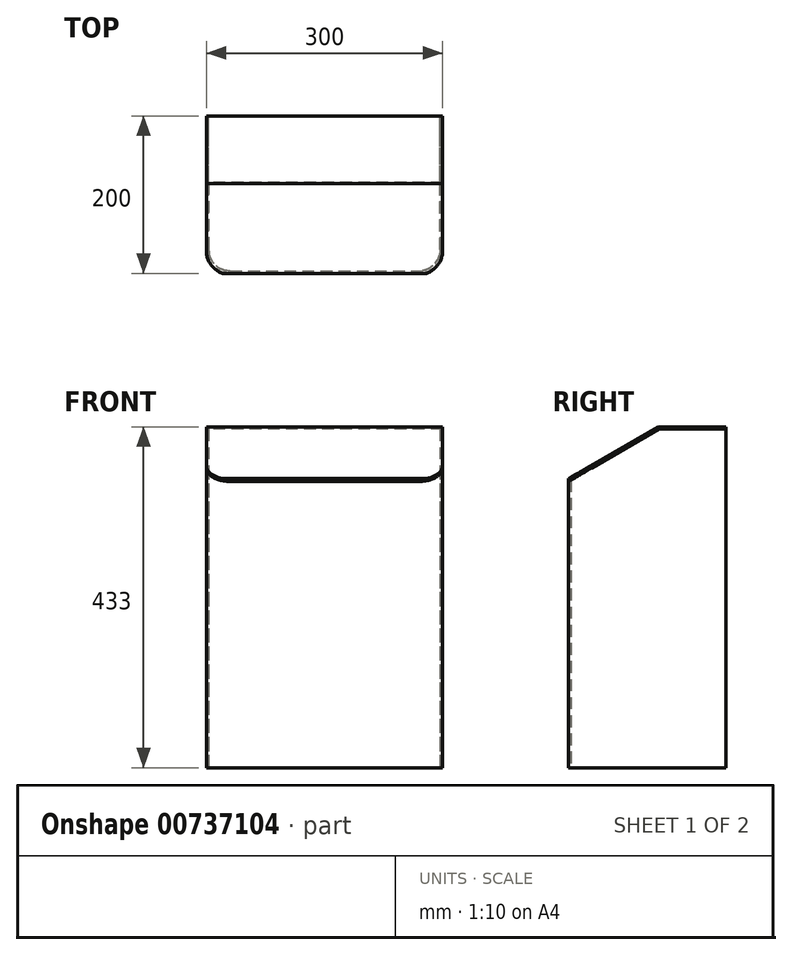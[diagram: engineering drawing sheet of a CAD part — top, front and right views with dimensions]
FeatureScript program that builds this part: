
annotation { "Feature Type Name" : "Feature", "Feature Type Description" : "" }
export const myFeature = defineFeature(function(context is Context, id is Id, definition is map)
    precondition{}
    {
        {
            var Q0;
            Q0=qCreatedBy(makeId("Top.planeOp"),FACE);
            var sketch = newSketch(context, id + "F0", { "sketchPlane" : qUnion([Q0])});
            skLineSegment(sketch, "E0", {"start": v(-30, 0) * mm, "end": v(-270, 0) * mm});
            skLineSegment(sketch, "E1", {"start": v(-300, 30) * mm, "end": v(-300, 200) * mm});
            skLineSegment(sketch, "E2", {"start": v(0, 30) * mm, "end": v(0, 200) * mm});
            skPoint(sketch, "E3.visualSharp", {"position": v(-300, 0) * mm});
            skArc(sketch, "E3.filletArc", {"start": v(-300, 30) * mm, "mid": v(-291.21, 8.79) * mm, "end": v(-270, 0) * mm});
            skPoint(sketch, "E4.visualSharp", {"position": v(0, 0) * mm});
            skArc(sketch, "E4.filletArc", {"start": v(-30, 0) * mm, "mid": v(-8.79, 8.79) * mm, "end": v(0, 30) * mm});
            skLineSegment(sketch, "E5.0", {"start": v(-297, 30) * mm, "end": v(-297, 200) * mm});
            skLineSegment(sketch, "E5.1", {"start": v(-3, 30) * mm, "end": v(-3, 200) * mm});
            skArc(sketch, "E5.2", {"start": v(-30, 3) * mm, "mid": v(-10.9, 10.9) * mm, "end": v(-3, 30) * mm});
            skLineSegment(sketch, "E5.3", {"start": v(-30, 3) * mm, "end": v(-270, 3) * mm});
            skArc(sketch, "E5.4", {"start": v(-297, 30) * mm, "mid": v(-289.1, 10.9) * mm, "end": v(-270, 3) * mm});
            skLineSegment(sketch, "E6", {"start": v(-300, 200) * mm, "end": v(-297, 200) * mm});
            skLineSegment(sketch, "E7", {"start": v(0, 200) * mm, "end": v(-3, 200) * mm});
            skSolve(sketch);
        }
        {
            var Q0;
            Q0=makeQuery(id+"F0.imprint","IMPRINT",FACE,{"disambiguationData":[TD([[makeQuery(id+"F0.imprint","IMPRINT",EDGE,{"derivedFrom":sQuery(id+"F0.wireOp",EDGE,"E0")}),-1.0]])]});
            extrude(context, id + "F1", {"entities" : qUnion([Q0]), "depth" : 430 * mm, "offsetDistance" : 25 * mm});
        }
        {
            var Q0;
            Q0=makeQuery(id+"F1.opExtrude","SWEPT_FACE",FACE,{"disambiguationData":[OSD([sQuery(id+"F0.wireOp",EDGE,"E1")])]});
            var sketch = newSketch(context, id + "F2", { "sketchPlane" : qUnion([Q0])});
            skLineSegment(sketch, "E8", {"start": v(-115, 430) * mm, "end": v(118.7, 430) * mm});
            skLineSegment(sketch, "E9", {"start": v(-115, 430) * mm, "end": v(118.7, 295.08) * mm});
            skLineSegment(sketch, "E10", {"start": v(118.7, 295.08) * mm, "end": v(118.7, 430) * mm});
            skSolve(sketch);
        }
        {
            var Q0;
            {var subQ3=sQuery(id+"F2.wireOp",EDGE,"E10");Q0=makeQuery(id+"F2.imprint","IMPRINT",FACE,{"disambiguationData":[TD([[makeQuery(id+"F2.imprint","IMPRINT",EDGE,{"derivedFrom":subQ3}),1.0]])]});}
            var Q1;
            {var subQ0=sQuery(id+"F2.wireOp",EDGE,"E8");var subQ1=sQuery(id+"F0.wireOp",EDGE,"E1");var subQ4=sQuery(id+"F2.wireOp",EDGE,"E9");var subQ5=makeQuery(id+"F2.imprint","INTERSECT",VERTEX,{"derivedFrom":[makeQuery(id+"F1.opExtrude","CAP_EDGE",EDGE,{"disambiguationData":[OSD([subQ1])],"isStart":false}),subQ0,subQ4]});Q1=makeQuery(id+"F2.imprint","IMPRINT",FACE,{"disambiguationData":[TD([[makeQuery(id+"F2.imprint","IMPRINT",EDGE,{"disambiguationData":[TD([[subQ5,1.0]])],"derivedFrom":subQ0}),1.0]])]});}
            extrude(context, id + "F3", {"entities" : qUnion([Q0, Q1]), "operationType" : NewBodyOperationType.REMOVE, "oppositeDirection" : true, "depth" : 455 * mm, "offsetDistance" : 25 * mm});
        }
        {
            var Q0;
            Q0=makeQuery(id+"F1.opExtrude","SWEPT_FACE",FACE,{"disambiguationData":[OSD([sQuery(id+"F0.wireOp",EDGE,"E1")])]});
            var sketch = newSketch(context, id + "F4", { "sketchPlane" : qUnion([Q0])});
            skLineSegment(sketch, "E11.0", {"start": v(-115, 430) * mm, "end": v(-200, 430) * mm});
            skLineSegment(sketch, "E11.1", {"start": v(-115, 430) * mm, "end": v(-30, 380.93) * mm});
            skLineSegment(sketch, "E11.2", {"start": v(0, 363.6) * mm, "end": v(-30, 380.93) * mm});
            skLineSegment(sketch, "E12", {"start": v(-200, 430) * mm, "end": v(-200, 433) * mm});
            skLineSegment(sketch, "E13.0", {"start": v(-114.2, 433) * mm, "end": v(-200, 433) * mm});
            skLineSegment(sketch, "E13.1", {"start": v(-114.2, 433) * mm, "end": v(-28.5, 383.52) * mm});
            skLineSegment(sketch, "E13.2", {"start": v(0, 367.07) * mm, "end": v(-28.5, 383.52) * mm});
            skLineSegment(sketch, "E14", {"start": v(0, 363.6) * mm, "end": v(0, 367.07) * mm});
            skSolve(sketch);
        }
        {
            var Q0;
            Q0=makeQuery(id+"F4.imprint","IMPRINT",FACE,{"disambiguationData":[TD([[makeQuery(id+"F4.imprint","IMPRINT",EDGE,{"derivedFrom":sQuery(id+"F4.wireOp",EDGE,"E11.0")}),-1.0]])]});
            extrude(context, id + "F5", {"entities" : qUnion([Q0]), "oppositeDirection" : true, "depth" : 300 * mm, "offsetDistance" : 25 * mm});
        }
        {
            var Q0;
            Q0=makeQuery(id+"F5.opExtrude","SWEPT_FACE",FACE,{"disambiguationData":[OSD([sQuery(id+"F4.wireOp",EDGE,"E11.1"),sQuery(id+"F4.wireOp",EDGE,"E11.2")])]});
            var sketch = newSketch(context, id + "F6", { "sketchPlane" : qUnion([Q0])});
            skEllipticalArc(sketch, "E15.0", {});
            skEllipticalArc(sketch, "E15.1", {});
            const initialGuessF6  = {"E15.0": [-0.27, -0.216443375672974, 0, 1, 0.03464101615137754, 0.03, 0, 1.5707963267948966], "E15.1": [-0.03, -0.21644337567297406, 0, 1, 0.03464101615137754, 0.03, 4.71238898038469, 0]};
            skSetInitialGuess(sketch, initialGuessF6);
            skSolve(sketch);
        }
        {
            var Q0;
            {var subQ0=sQuery(id+"F6.wireOp",EDGE,"E15.1");Q0=makeQuery(id+"F6.imprint","IMPRINT",FACE,{"disambiguationData":[TD([[makeQuery(id+"F6.imprint","IMPRINT",EDGE,{"derivedFrom":subQ0}),-1.0]])]});}
            var Q1;
            {var subQ0=sQuery(id+"F6.wireOp",EDGE,"E15.0");Q1=makeQuery(id+"F6.imprint","IMPRINT",FACE,{"disambiguationData":[TD([[makeQuery(id+"F6.imprint","IMPRINT",EDGE,{"derivedFrom":subQ0}),-1.0]])]});}
            extrude(context, id + "F7", {"entities" : qUnion([Q0, Q1]), "operationType" : NewBodyOperationType.REMOVE, "oppositeDirection" : true, "depth" : 16 * mm, "offsetDistance" : 25 * mm});
        }
    });
